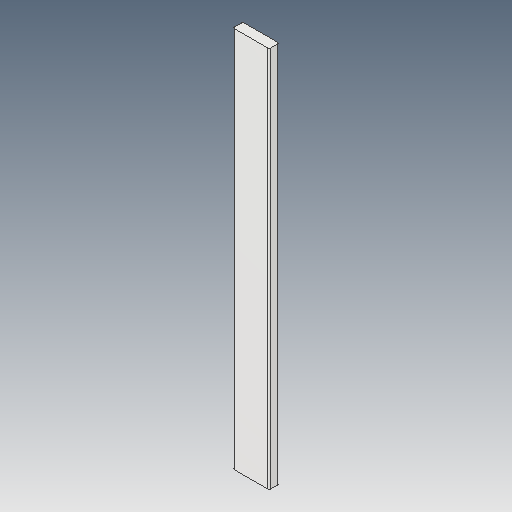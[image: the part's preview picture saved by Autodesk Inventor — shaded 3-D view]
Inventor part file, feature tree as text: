
AUTODESK INVENTOR PART (.ipt)
format: ipt  version: 2023.5 (Build 275446000, 446)  size: 83,456 bytes
history: native  units: in
note: dims shown in document units (in); Inventor stores cm internally (conversion verified against a paired STEP export)
features: fillet x1
ambient origin geometry x8: Origin, YZ Plane, XZ Plane, XY Plane, X Axis, Y Axis, Z Axis, Center Point
bodies: Solid1 (feature_tree)
feature tree (1):
  fillet  "Fillet1"  [1 undecoded]
note: 1 required parameter value undecoded (feature->parameter linkage not recoverable at this tier; creation-order binding heuristic only, values carry confidence <= 0.55)
